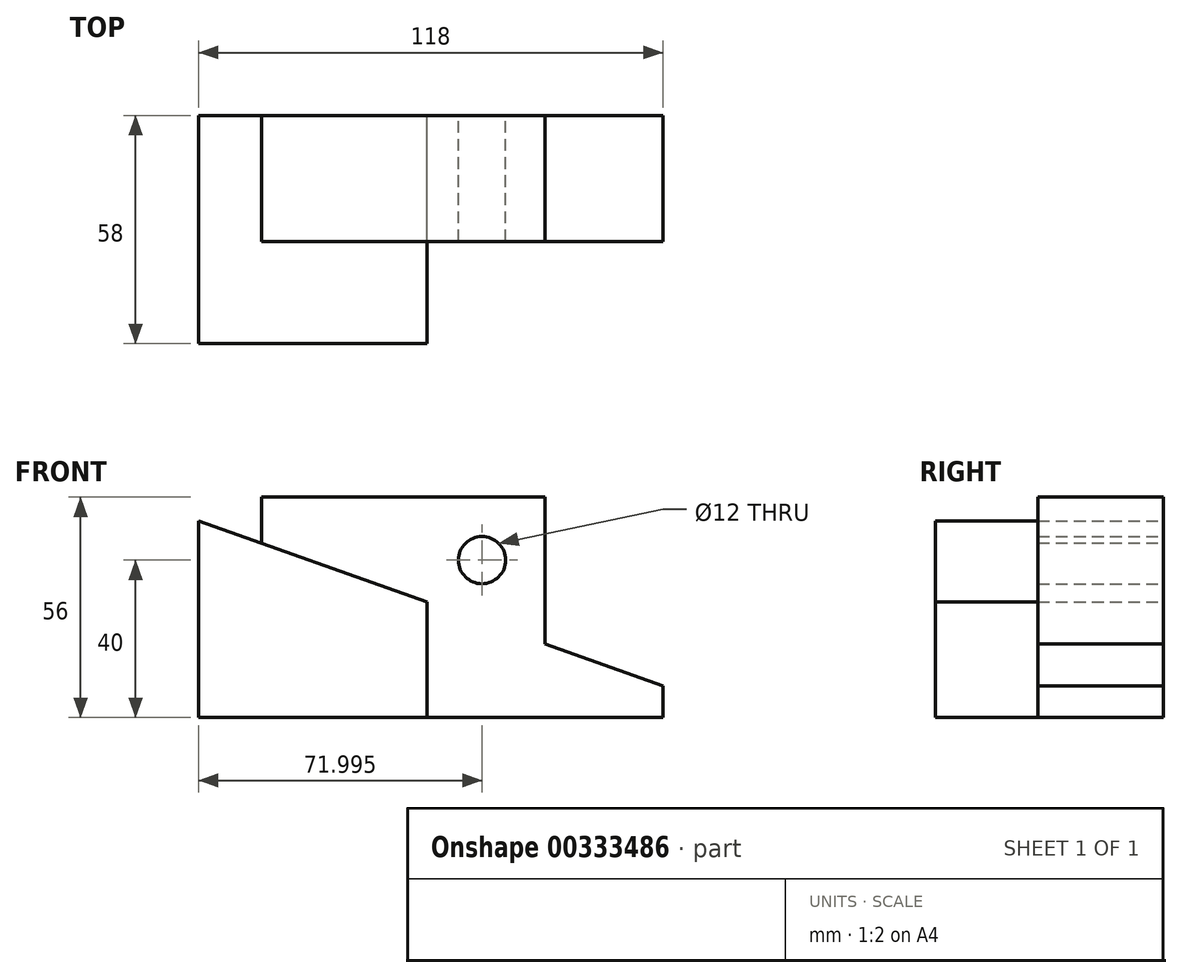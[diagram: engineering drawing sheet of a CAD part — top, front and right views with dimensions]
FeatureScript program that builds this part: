
annotation { "Feature Type Name" : "Feature", "Feature Type Description" : "" }
export const myFeature = defineFeature(function(context is Context, id is Id, definition is map)
    precondition{}
    {
        {
            var Q0;
            Q0=qCreatedBy(makeId("Front.planeOp"),FACE);
            var sketch = newSketch(context, id + "F0", { "sketchPlane" : qUnion([Q0])});
            skLineSegment(sketch, "E0", {"start": v(66.34, 0) * mm, "end": v(66.34, 8) * mm});
            skLineSegment(sketch, "E1", {"start": v(-51.66, 50) * mm, "end": v(-51.66, 0) * mm});
            skLineSegment(sketch, "E2", {"start": v(-51.66, 0) * mm, "end": v(66.34, 0) * mm});
            skLineSegment(sketch, "E3", {"start": v(-51.66, 50) * mm, "end": v(6.34, 29.36) * mm});
            skLineSegment(sketch, "E4", {"start": v(6.34, 0) * mm, "end": v(6.34, 29.36) * mm});
            skLineSegment(sketch, "E5", {"start": v(36.34, 18.68) * mm, "end": v(36.34, 56) * mm});
            skLineSegment(sketch, "E6", {"start": v(36.34, 56) * mm, "end": v(-35.66, 56) * mm});
            skLineSegment(sketch, "E7", {"start": v(-35.66, 56) * mm, "end": v(-35.66, 44.3) * mm});
            skLineSegment(sketch, "E8.trimOffspring", {"start": v(36.34, 18.68) * mm, "end": v(66.34, 8) * mm});
            skCircle(sketch, "E9", {"center": v(20.34, 40) * mm, "radius": 6 * mm});
            skSolve(sketch);
        }
        {
            var Q0;
            {var subQ3=sQuery(id+"F0.wireOp",EDGE,"E1");Q0=makeQuery(id+"F0.imprint","IMPRINT",FACE,{"disambiguationData":[TD([[makeQuery(id+"F0.imprint","IMPRINT",EDGE,{"derivedFrom":subQ3}),1.0]])]});}
            extrude(context, id + "F1", {"entities" : qUnion([Q0]), "depth" : 58 * mm});
        }
        {
            var Q0;
            {var subQ2=sQuery(id+"F0.wireOp",EDGE,"E0");Q0=makeQuery(id+"F0.imprint","IMPRINT",FACE,{"disambiguationData":[TD([[makeQuery(id+"F0.imprint","IMPRINT",EDGE,{"derivedFrom":subQ2}),1.0]])]});}
            extrude(context, id + "F2", {"entities" : qUnion([Q0]), "depth" : 32 * mm});
        }
    });
